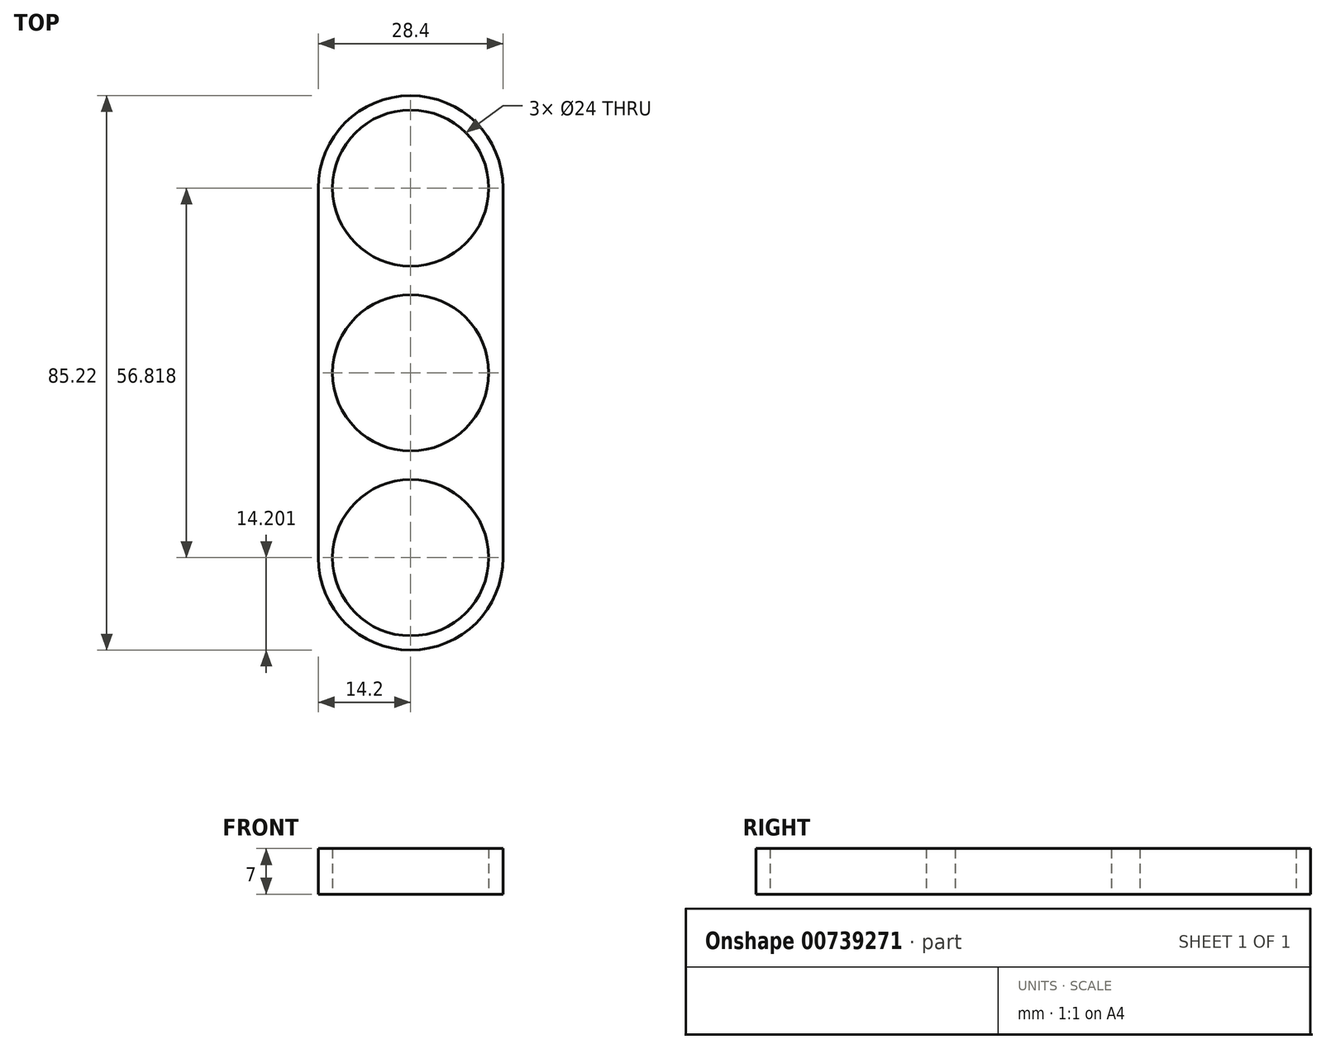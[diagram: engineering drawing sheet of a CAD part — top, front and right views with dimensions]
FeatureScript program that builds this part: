
annotation { "Feature Type Name" : "Feature", "Feature Type Description" : "" }
export const myFeature = defineFeature(function(context is Context, id is Id, definition is map)
    precondition{}
    {
        {
            var Q0;
            Q0=qCreatedBy(makeId("Top.planeOp"),FACE);
            var sketch = newSketch(context, id + "F0", { "sketchPlane" : qUnion([Q0])});
            skCircle(sketch, "E0", {"center": v(0, 0) * mm, "radius": 12 * mm});
            skCircle(sketch, "E1", {"center": v(0, 28.4) * mm, "radius": 12 * mm});
            skArc(sketch, "E2", {"start": v(14.2, 28.4) * mm, "mid": v(0, 42.6) * mm, "end": v(-14.2, 28.4) * mm});
            skArc(sketch, "E3.1.0", {"start": v(-14.2, -28.4) * mm, "mid": v(0, -42.6) * mm, "end": v(14.2, -28.4) * mm});
            skCircle(sketch, "E3.1.1", {"center": v(0, -28.4) * mm, "radius": 12 * mm});
            skLineSegment(sketch, "E4", {"start": v(-14.2, 28.4) * mm, "end": v(-14.2, -28.4) * mm});
            skLineSegment(sketch, "E5", {"start": v(14.2, 28.4) * mm, "end": v(14.2, -28.4) * mm});
            skSolve(sketch);
        }
        {
            var Q0;
            Q0=makeQuery(id+"F0.imprint","IMPRINT",FACE,{"disambiguationData":[TD([[makeQuery(id+"F0.imprint","IMPRINT",EDGE,{"derivedFrom":sQuery(id+"F0.wireOp",EDGE,"E0")}),-1.0]])]});
            extrude(context, id + "F1", {"entities" : qUnion([Q0]), "depth" : 7 * mm, "offsetDistance" : 25 * mm});
        }
    });
